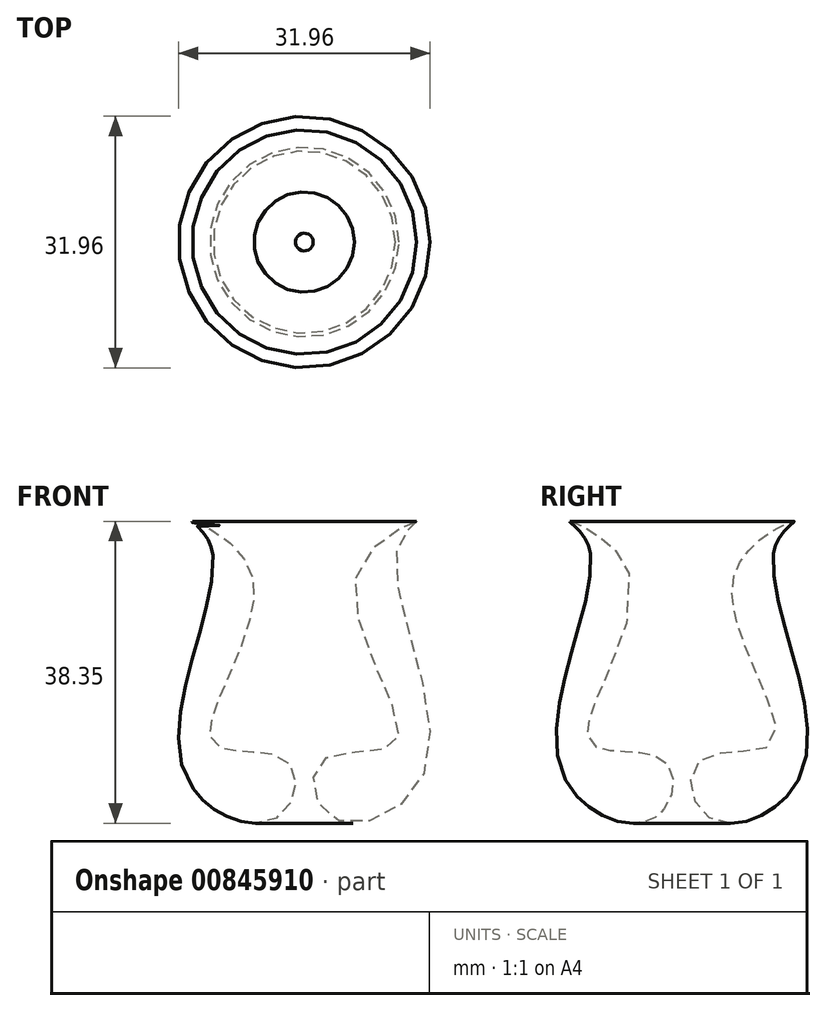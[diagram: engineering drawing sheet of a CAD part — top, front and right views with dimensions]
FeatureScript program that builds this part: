
annotation { "Feature Type Name" : "Feature", "Feature Type Description" : "" }
export const myFeature = defineFeature(function(context is Context, id is Id, definition is map)
    precondition{}
    {
        {
            var Q0;
            Q0=qCreatedBy(makeId("Front.planeOp"),FACE);
            var sketch = newSketch(context, id + "F0", { "sketchPlane" : qUnion([Q0])});
            skFitSpline(sketch, "E0", {"points": [v(14.25, 37.69) * mm, v(11.8, 34.32) * mm, v(15.47, 6.43) * mm, v(3.52, 0) * mm, v(2.3, 7.35) * mm, v(11.8, 9.8) * mm, v(6.59, 30.64) * mm, v(14.25, 37.69) * mm]});
            skLineSegment(sketch, "E1", {"start": v(0, 48.41) * mm, "end": v(0, -24.51) * mm});
            skSolve(sketch);
        }
        {
            var Q0;
            Q0=makeQuery(id+"F0.imprint","IMPRINT",FACE,{"disambiguationData":[TD([[makeQuery(id+"F0.imprint","IMPRINT",EDGE,{"derivedFrom":sQuery(id+"F0.wireOp",EDGE,"E0")}),-1.0]])]});
            var Q1;
            Q1=sQuery(id+"F0.wireOp",EDGE,"E1");
            revolve(context, id + "F1", {"surfaceOperationType" : NewSurfaceOperationType.NEW, "entities" : qUnion([Q0]), "axis" : qUnion([Q1]), "revolveType" : RevolveType.FULL});
        }
    });
